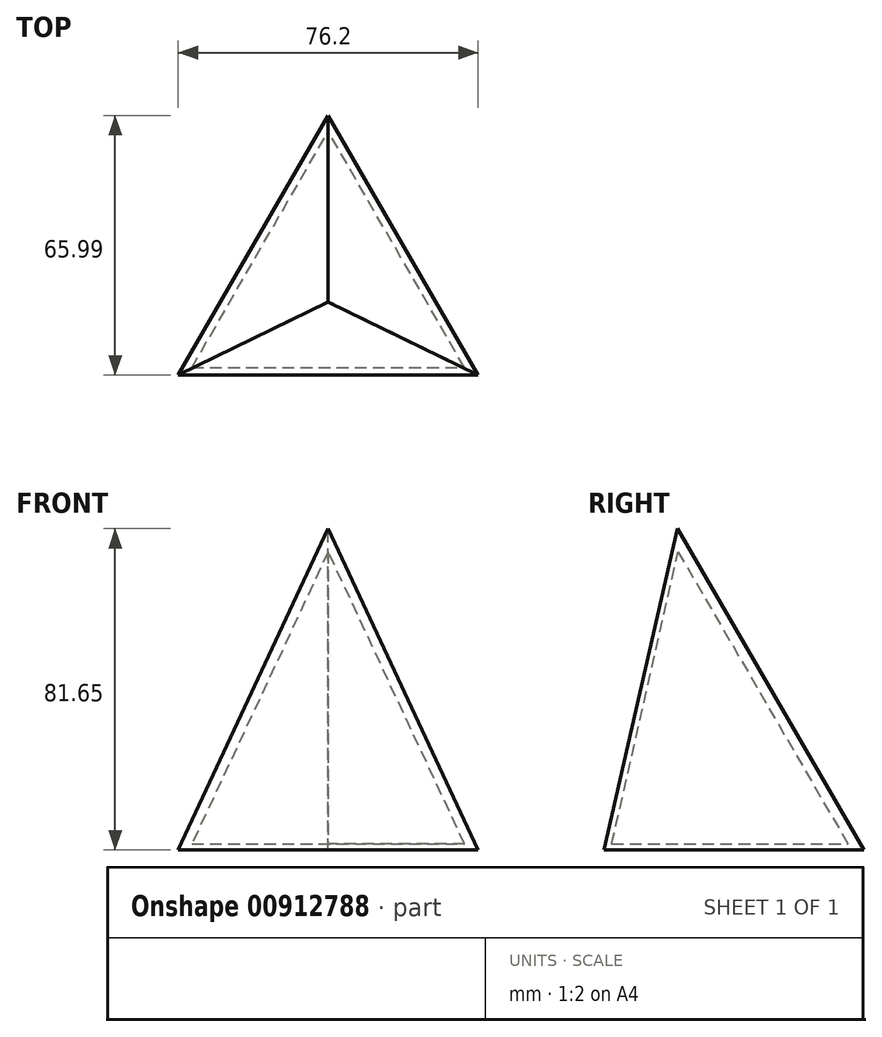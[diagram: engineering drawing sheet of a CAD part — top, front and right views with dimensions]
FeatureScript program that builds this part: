
annotation { "Feature Type Name" : "Feature", "Feature Type Description" : "" }
export const myFeature = defineFeature(function(context is Context, id is Id, definition is map)
    precondition{}
    {
        {
            var Q0;
            Q0=qCreatedBy(makeId("Top.planeOp"),FACE);
            var sketch = newSketch(context, id + "F0", { "sketchPlane" : qUnion([Q0])});
            skLineSegment(sketch, "E0", {"start": v(38.1, -18.56) * mm, "end": v(0, 47.43) * mm});
            skLineSegment(sketch, "E1", {"start": v(-38.1, -18.56) * mm, "end": v(0, 47.43) * mm});
            skLineSegment(sketch, "E2", {"start": v(-38.1, -18.56) * mm, "end": v(38.1, -18.56) * mm});
            skSolve(sketch);
        }
        {
            var Q0;
            Q0=qCreatedBy(makeId("Right.planeOp"),FACE);
            var sketch = newSketch(context, id + "F1", { "sketchPlane" : qUnion([Q0])});
            skLineSegment(sketch, "E3", {"start": v(0, 0) * mm, "end": v(0, 81.65) * mm});
            skSolve(sketch);
        }
        {
            var Q0;
            Q0=makeQuery(id+"F0.imprint","IMPRINT",FACE,{"disambiguationData":[TD([[makeQuery(id+"F0.imprint","IMPRINT",EDGE,{"derivedFrom":sQuery(id+"F0.wireOp",EDGE,"E0")}),1.0]])]});
            var Q1;
            Q1=sQuery(id+"F1.wireOp",VERTEX,"E3.end");
            loft(context, id + "F2", {"sheetProfilesArray" : [{ "sheetProfileEntities" : qUnion([Q0]) }, { "sheetProfileEntities" : qUnion([Q1]) }]});
        }
        {
            var Q0;
            Q0=makeQuery(id+"F2.opLoft","CAP_FACE",FACE,{"disambiguationData":[OSD([makeQuery(id+"F0.imprint","IMPRINT",FACE,{"disambiguationData":[TD([[makeQuery(id+"F0.imprint","IMPRINT",EDGE,{"derivedFrom":sQuery(id+"F0.wireOp",EDGE,"E0")}),1.0]])]})])],"isStart":true});
            var Q1;
            Q1=makeQuery(id+"F2.opLoft","SWEPT_BODY",BODY,{"disambiguationData":[OSD([makeQuery(id+"F0.imprint","IMPRINT",FACE,{"disambiguationData":[TD([[makeQuery(id+"F0.imprint","IMPRINT",EDGE,{"derivedFrom":sQuery(id+"F0.wireOp",EDGE,"E0")}),1.0]])]}),sQuery(id+"F1.wireOp",VERTEX,"E3.end")])]});
            shell(context, id + "F3", {"isHollow" : true, "entities" : qUnion([Q0]), "parts" : qUnion([Q1]), "thickness" : 1.52 * mm});
        }
    });
